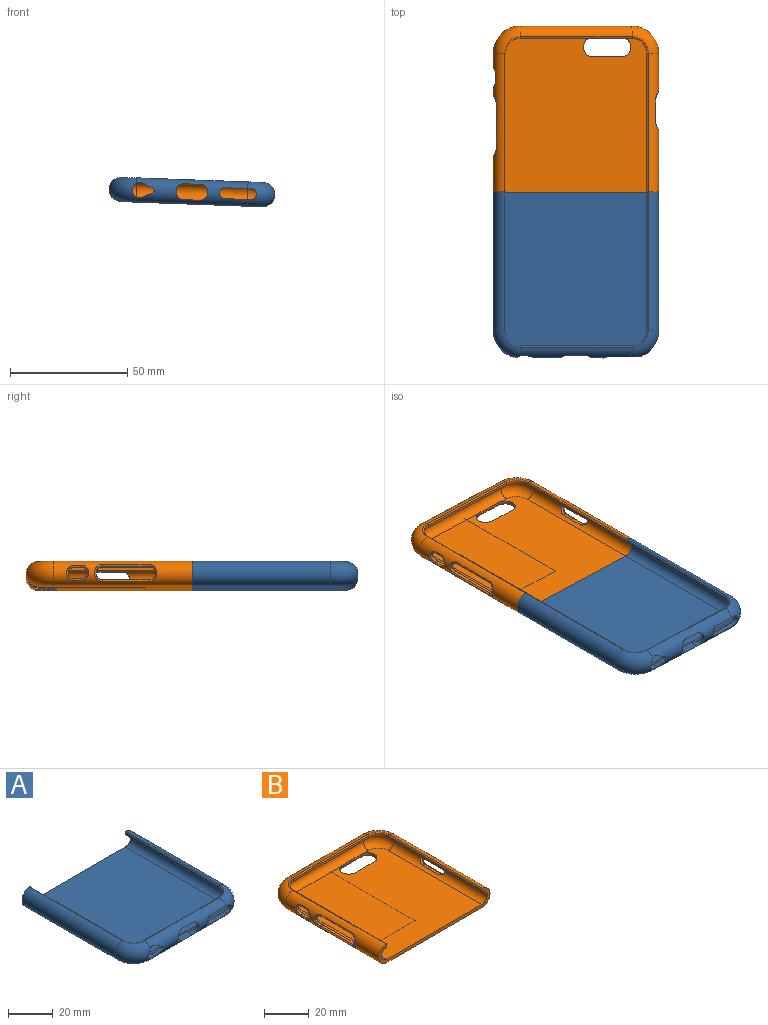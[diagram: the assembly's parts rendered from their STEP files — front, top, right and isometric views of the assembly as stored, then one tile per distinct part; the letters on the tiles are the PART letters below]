
ASSEMBLY  parts=2 mates=3
PART A: 35 faces, bbox 72.6x71.8x10.4 mm
  f0: plane 47.52x1.24mm, normal (0,1,0), area 59mm2, adj f13,f14,f16,f18
  f1: cylinder r=2.32mm len=4.65mm, axis (0,1,0), area 14.2mm2, adj f10,f12,f14,f20
  f2: plane 4.25x3.36mm, normal (-0.43,0,0.9), area 9.7mm2, adj f3,f5,f14,f20
  f3: cylinder r=1mm len=1.9mm, axis (0,1,0), area 4mm2, adj f2,f4,f14,f20
  f4: plane 4.25x3.35mm, normal (-0.43,0,-0.9), area 9.7mm2, adj f3,f5,f14,f20
  f5: cylinder r=3.25mm len=6.5mm, axis (0,1,0), area 31.1mm2, adj f2,f4,f14,f17,f19,f20
  f6: cylinder r=3.4mm len=6.8mm, axis (0,1,0), area 25.3mm2, adj f7,f9,f14,f20
  f7: plane 6.85x3.56mm, normal (0,0,1), area 24.4mm2, adj f6,f8,f14,f20
  f8: cylinder r=3.4mm len=6.8mm, axis (0,1,0), area 25.3mm2, adj f7,f9,f14,f20
  f9: plane 6.85x3.49mm, normal (0,0,-1), area 23.9mm2, adj f6,f8,f14,f20
  f10: plane 11.25x2.27mm, normal (0,0,1), area 24.1mm2, adj f1,f11,f14,f15,f20,f21
  f11: cylinder r=2.32mm len=4.65mm, axis (0,1,0), area 14.8mm2, adj f10,f12,f15,f21
  f12: plane 11.25x2.26mm, normal (0,0,-1), area 24.1mm2, adj f1,f11,f14,f15,f20,f21
  f13: cylinder r=0.51mm len=47.52mm, axis (-1,0,0), area 40.5mm2, adj f0,f20,f22,f23
  f14: cylinder r=3.43mm len=47.52mm, axis (-1,0,0), area 297mm2, adj f0,f1,f2,f3,f4,f5,f6,f7
  f15: torus R=6.37mm, axis (0,0,-1), area 127.5mm2, adj f10,f11,f12,f14,f16,f32,f33
  f16: cylinder r=6.37mm len=6.37mm, axis (0,0,-1), area 12.4mm2, adj f0,f15,f22,f31
  f17: torus R=6.37mm, axis (0,0,-1), area 136.6mm2, adj f5,f14,f18,f30,f33
  f18: cylinder r=6.37mm len=6.37mm, axis (0,0,-1), area 12.4mm2, adj f0,f17,f23,f29
  f19: torus R=6.37mm, axis (0,0,-1), area 235.3mm2, adj f5,f20,f23,f25,f26
  f20: cylinder r=5.2mm len=47.52mm, axis (-1,0,0), area 567.6mm2, adj f1,f2,f3,f4,f5,f6,f7,f8
  f21: torus R=6.37mm, axis (0,0,-1), area 226.6mm2, adj f10,f11,f12,f20,f22,f25,f28
  f22: torus R=6.88mm, axis (0,0,1), area 8.8mm2, adj f13,f16,f21,f27
  f23: torus R=6.88mm, axis (0,0,1), area 8.8mm2, adj f13,f18,f19,f24
  f24: cylinder r=0.51mm len=59.27mm, axis (0,1,0), area 50.6mm2, adj f23,f26,f29,f34
  f25: plane 65.64x60.26mm, normal (0,0,-1), area 3938.2mm2, adj f19,f20,f21,f26,f28,f34
  f26: cylinder r=5.2mm len=59.27mm, axis (0,1,0), area 935.4mm2, adj f19,f24,f25,f34
  f27: cylinder r=0.51mm len=59.27mm, axis (0,-1,0), area 50.6mm2, adj f22,f28,f31,f34
  f28: cylinder r=5.2mm len=59.27mm, axis (0,-1,0), area 935.4mm2, adj f21,f25,f27,f34
  f29: plane 59.27x1.24mm, normal (1,0,0), area 73.6mm2, adj f18,f24,f30,f34
  f30: cylinder r=3.43mm len=59.27mm, axis (0,1,0), area 637.7mm2, adj f17,f29,f33,f34
  f31: plane 59.27x1.24mm, normal (-1,0,0), area 73.6mm2, adj f16,f27,f32,f34
  f32: cylinder r=3.43mm len=59.27mm, axis (0,-1,0), area 637.7mm2, adj f15,f31,f33,f34
  f33: plane 65.64x60.26mm, normal (0,0,1), area 3938.2mm2, adj f14,f15,f17,f30,f32,f34
  f34: plane 70.67x10.38mm, normal (0,1,0), area 155.2mm2, adj f24,f25,f26,f27,f28,f29,f30,f31
PART B: 66 faces, bbox 72.6x71.8x10.4 mm
  f0: plane 65.64x60.26mm, normal (0,0,-1), area 3189.3mm2, adj f1,f8,f9,f18,f19,f20,f25,f26
  f1: cylinder r=5.2mm len=5.46mm, axis (1,0,0), area 11.3mm2, adj f0,f2,f20,f63
  f2: plane 55.37x24.66mm, normal (0,0,1), area 756.9mm2, adj f1,f19,f20,f59,f60,f61,f63,f64
  f3: plane 65.64x60.26mm, normal (0,0,1), area 3790.2mm2, adj f4,f6,f12,f13,f16,f21,f22,f23
  f4: cylinder r=3.43mm len=59.27mm, axis (0,-1,0), area 543.7mm2, adj f3,f5,f13,f42,f43,f44,f45,f58
  f5: plane 59.27x1.24mm, normal (-1,0,0), area 73.6mm2, adj f4,f10,f14,f58
  f6: cylinder r=3.43mm len=59.27mm, axis (0,1,0), area 440.9mm2, adj f3,f7,f16,f34,f35,f36,f37,f38
  f7: plane 59.27x1.24mm, normal (1,0,0), area 73.6mm2, adj f6,f11,f17,f58
  f8: cylinder r=5.2mm len=59.27mm, axis (0,-1,0), area 811.7mm2, adj f0,f10,f18,f46,f47,f48,f49,f58
  f9: cylinder r=5.2mm len=59.27mm, axis (0,1,0), area 675.9mm2, adj f0,f11,f20,f50,f51,f52,f53,f54
  f10: cylinder r=0.51mm len=59.27mm, axis (0,-1,0), area 50.6mm2, adj f5,f8,f31,f58
  f11: cylinder r=0.51mm len=59.27mm, axis (0,1,0), area 50.6mm2, adj f7,f9,f33,f58
  f12: cylinder r=3.43mm len=47.52mm, axis (1,0,0), area 507.7mm2, adj f3,f13,f15,f16,f21,f23,f24
  f13: torus R=6.37mm, axis (0,0,-1), area 144.5mm2, adj f3,f4,f12,f14
  f14: cylinder r=6.37mm len=6.37mm, axis (0,0,-1), area 12.4mm2, adj f5,f13,f15,f31
  f15: plane 47.52x1.24mm, normal (0,-1,0), area 59mm2, adj f12,f14,f17,f32
  f16: torus R=6.37mm, axis (0,0,-1), area 144.5mm2, adj f3,f6,f12,f17
  f17: cylinder r=6.37mm len=6.37mm, axis (0,0,-1), area 12.4mm2, adj f7,f15,f16,f33
  f18: torus R=6.37mm, axis (0,0,-1), area 242.7mm2, adj f0,f8,f19,f31
  f19: cylinder r=5.2mm len=47.52mm, axis (1,0,0), area 646.2mm2, adj f0,f2,f18,f20,f28,f29,f30,f32
  f20: torus R=6.37mm, axis (0,0,-1), area 240.7mm2, adj f0,f1,f2,f9,f19,f33,f59,f62
  f21: cylinder r=4.1mm len=8.2mm, axis (0,0,1), area 16.3mm2, adj f3,f12,f22,f24,f27,f29
  f22: plane 12.06x1.27mm, normal (0,1,0), area 15.3mm2, adj f3,f21,f23,f25
  f23: cylinder r=4.1mm len=8.2mm, axis (0,0,1), area 16.3mm2, adj f3,f12,f22,f24,f26,f28
  f24: plane 12.06x1.22mm, normal (0,-1,0), area 14.7mm2, adj f12,f21,f23,f30
  f25: cylinder r=0.51mm len=12.06mm, axis (1,0,0), area 9.6mm2, adj f0,f22,f26,f27
  f26: torus R=4.61mm, axis (0,0,-1), area 8.7mm2, adj f0,f23,f25,f28
  f27: torus R=4.61mm, axis (0,0,-1), area 8.7mm2, adj f0,f21,f25,f29
  f28: bspline ~4.26x1.79mm, area 2.1mm2, adj f19,f23,f26,f30
  f29: bspline ~4.26x1.79mm, area 2.1mm2, adj f19,f21,f27,f30
  f30: cylinder r=0.51mm len=12.06mm, axis (1,0,0), area 10.6mm2, adj f19,f24,f28,f29
  f31: torus R=6.88mm, axis (0,0,1), area 8.8mm2, adj f10,f14,f18,f32
  f32: cylinder r=0.51mm len=47.52mm, axis (1,0,0), area 40.5mm2, adj f15,f19,f31,f33
  f33: torus R=6.88mm, axis (0,0,1), area 8.8mm2, adj f11,f17,f20,f32
  f34: plane 3.63x1.25mm, normal (0,0,-1), area 4.5mm2, adj f6,f35,f37,f57
  f35: cylinder r=2.39mm len=4.77mm, axis (1,0,0), area 9.4mm2, adj f6,f34,f36,f55
  f36: plane 3.63x1.24mm, normal (0,0,1), area 4.5mm2, adj f6,f35,f37,f54
  f37: cylinder r=2.39mm len=4.77mm, axis (1,0,0), area 9.4mm2, adj f6,f34,f36,f56
  f38: plane 20.01x1.37mm, normal (0,0,-1), area 27.4mm2, adj f6,f39,f41,f53
  f39: cylinder r=2.8mm len=5.59mm, axis (1,0,0), area 11.4mm2, adj f6,f38,f40,f51
  f40: plane 20.01x1.35mm, normal (0,0,1), area 27mm2, adj f6,f39,f41,f50
  f41: cylinder r=2.8mm len=5.59mm, axis (1,0,0), area 11.4mm2, adj f6,f38,f40,f52
  f42: cylinder r=2.79mm len=5.59mm, axis (-1,0,0), area 11.4mm2, adj f4,f43,f45,f49
  f43: plane 10.2x1.37mm, normal (0,0,-1), area 13.9mm2, adj f4,f42,f44,f48
  f44: cylinder r=2.79mm len=5.59mm, axis (-1,0,0), area 11.4mm2, adj f4,f43,f45,f46
  f45: plane 10.2x1.35mm, normal (0,0,1), area 13.7mm2, adj f4,f42,f44,f47
  f46: bspline ~7.32x3.93mm, area 9.9mm2, adj f8,f44,f47,f48
  f47: cylinder r=0.51mm len=10.2mm, axis (0,-1,0), area 12.1mm2, adj f8,f45,f46,f49
  f48: cylinder r=0.51mm len=10.2mm, axis (0,-1,0), area 12.2mm2, adj f8,f43,f46,f49
  f49: bspline ~7.32x3.93mm, area 9.9mm2, adj f8,f42,f47,f48
  f50: cylinder r=0.51mm len=20.01mm, axis (0,1,0), area 23.8mm2, adj f9,f40,f51,f52
  f51: bspline ~7.33x3.94mm, area 9.9mm2, adj f9,f39,f50,f53
  f52: bspline ~7.33x3.93mm, area 9.9mm2, adj f9,f41,f50,f53
  f53: cylinder r=0.51mm len=20.01mm, axis (0,1,0), area 24mm2, adj f9,f38,f51,f52
  f54: cylinder r=0.51mm len=3.63mm, axis (0,1,0), area 4.1mm2, adj f9,f36,f55,f56
  f55: bspline ~6.42x3.47mm, area 8.2mm2, adj f9,f35,f54,f57
  f56: bspline ~6.42x3.47mm, area 8.2mm2, adj f9,f37,f54,f57
  f57: cylinder r=0.51mm len=3.63mm, axis (0,1,0), area 4.1mm2, adj f9,f34,f55,f56
  f58: plane 70.67x10.38mm, normal (0,-1,0), area 155.2mm2, adj f0,f3,f4,f5,f6,f7,f8,f9
  f59: plane 57.17x1.31mm, normal (1,0,0), area 71.6mm2, adj f2,f20,f60,f62
  f60: plane 24.66x1.27mm, normal (0,1,0), area 31.3mm2, adj f2,f59,f61,f62
  f61: plane 57.18x1.27mm, normal (-1,0,0), area 71.6mm2, adj f2,f19,f60,f62
  f62: plane 57.18x24.66mm, normal (0,0,-1), area 1410.1mm2, adj f19,f20,f59,f60,f61
  f63: plane 47.92x0.41mm, normal (1,0,0), area 19.2mm2, adj f0,f1,f2,f64
  f64: plane 12.7x0.41mm, normal (0,1,0), area 5.2mm2, adj f0,f2,f63,f65
  f65: plane 47.92x0.41mm, normal (-1,0,0), area 19.2mm2, adj f0,f2,f19,f64
PLACE A rot(axis=(0,1,0),2.1deg) t=(-1.57,6.58,-8.27)mm
PLACE B rot(axis=(0,1,0),2.1deg) t=(-1.57,6.58,-8.27)mm fixed
MATE planar B.f6 <-> A.f26  axis (0,-1,0) through (-31.5,6.58,-2.37)mm
MATE fastened B.f4 <-> A.f28  axis (0,-1,0) through (28.72,6.58,-4.59)mm
MATE cylindrical A.f26 <-> B.f6  axis (0,1,0) through (-31.5,6.58,-2.37)mm
